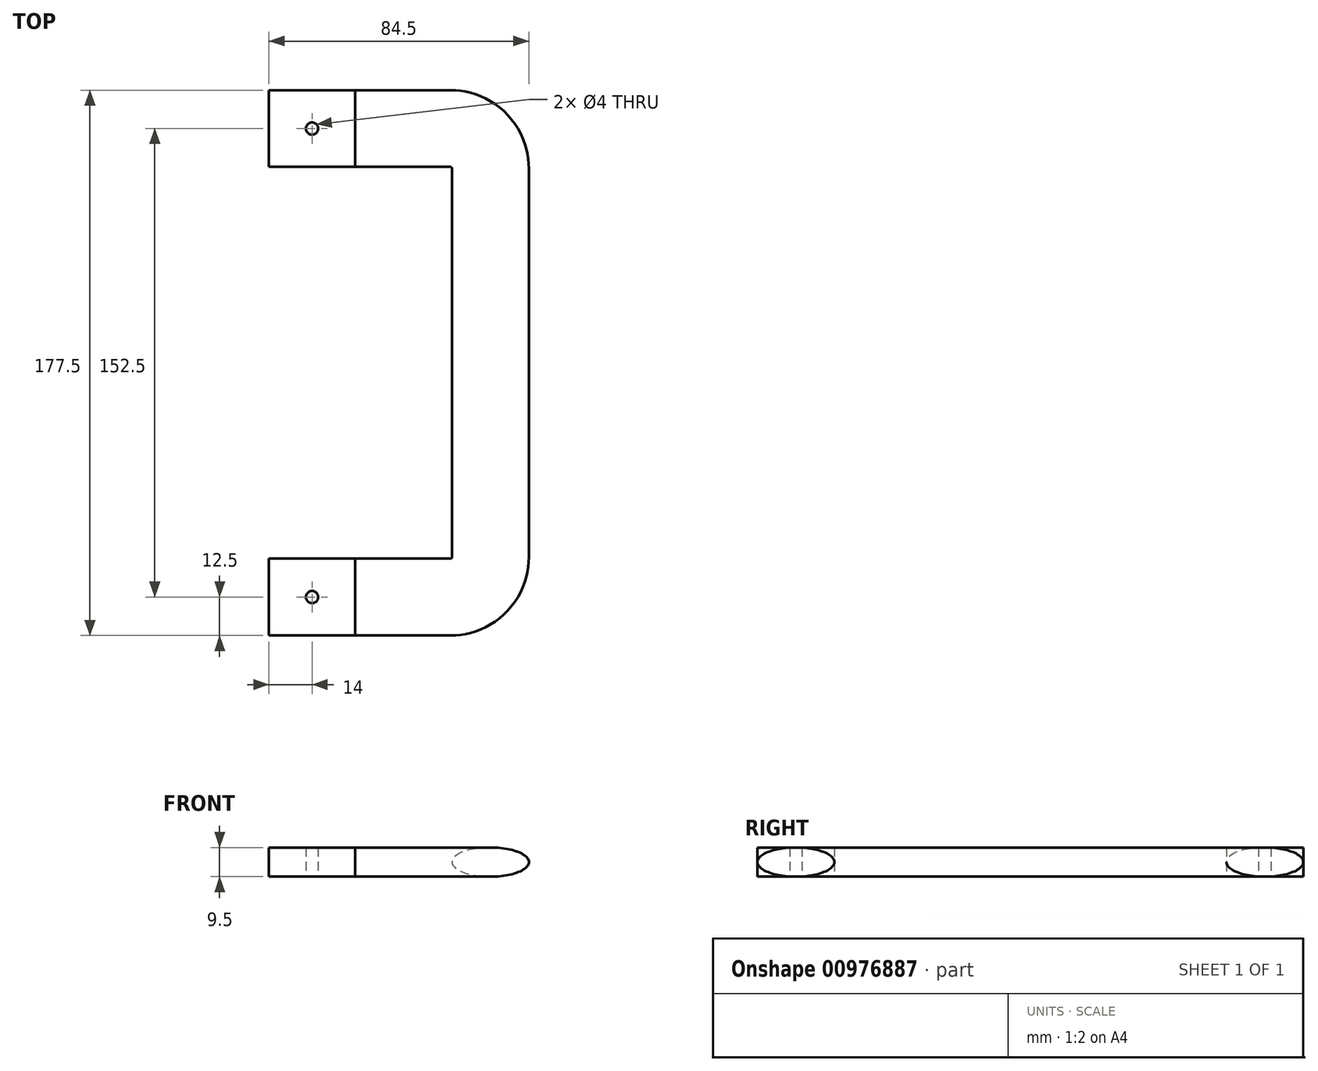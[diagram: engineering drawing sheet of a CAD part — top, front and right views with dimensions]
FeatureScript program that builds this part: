
annotation { "Feature Type Name" : "Feature", "Feature Type Description" : "" }
export const myFeature = defineFeature(function(context is Context, id is Id, definition is map)
    precondition{}
    {
        {
            var Q0;
            Q0=qCreatedBy(makeId("Top.planeOp"),FACE);
            var sketch = newSketch(context, id + "F0", { "sketchPlane" : qUnion([Q0])});
            skPoint(sketch, "E0", {"position": v(-44, 76.25) * mm});
            skPoint(sketch, "E1", {"position": v(-44, -76.25) * mm});
            skLineSegment(sketch, "E2.bottom", {"start": v(-30, 88.75) * mm, "end": v(-58, 88.75) * mm});
            skLineSegment(sketch, "E2.top", {"start": v(-30, 63.75) * mm, "end": v(-58, 63.75) * mm});
            skLineSegment(sketch, "E2.left", {"start": v(-30, 88.75) * mm, "end": v(-30, 63.75) * mm});
            skLineSegment(sketch, "E2.right", {"start": v(-58, 88.75) * mm, "end": v(-58, 63.75) * mm});
            skLineSegment(sketch, "E3.bottom", {"start": v(-30, -63.75) * mm, "end": v(-58, -63.75) * mm});
            skLineSegment(sketch, "E3.top", {"start": v(-30, -88.75) * mm, "end": v(-58, -88.75) * mm});
            skLineSegment(sketch, "E3.left", {"start": v(-30, -63.75) * mm, "end": v(-30, -88.75) * mm});
            skLineSegment(sketch, "E3.right", {"start": v(-58, -63.75) * mm, "end": v(-58, -88.75) * mm});
            skCircle(sketch, "E4", {"center": v(-44, 76.25) * mm, "radius": 2 * mm});
            skCircle(sketch, "E5", {"center": v(-44, -76.25) * mm, "radius": 2 * mm});
            skSolve(sketch);
        }
        {
            var Q0;
            Q0 = qSketchRegion(id + "F0", true);
            extrude(context, id + "F1", {"entities" : qUnion([Q0]), "endBound" : BoundingType.SYMMETRIC, "depth" : 9.5 * mm, "offsetDistance" : 25 * mm});
        }
        {
            var Q0;
            Q0=qCreatedBy(makeId("Top.planeOp"),FACE);
            var sketch = newSketch(context, id + "F2", { "sketchPlane" : qUnion([Q0])});
            skLineSegment(sketch, "E6", {"start": v(-30, 76.25) * mm, "end": v(1, 76.25) * mm});
            skLineSegment(sketch, "E7", {"start": v(14, 63.25) * mm, "end": v(14, -63.25) * mm});
            skLineSegment(sketch, "E8", {"start": v(1, -76.25) * mm, "end": v(-30, -76.25) * mm});
            skPoint(sketch, "E9.visualSharp", {"position": v(14, 76.25) * mm});
            skArc(sketch, "E9.filletArc", {"start": v(14, 63.25) * mm, "mid": v(10.2, 72.44) * mm, "end": v(1, 76.25) * mm});
            skPoint(sketch, "E10.visualSharp", {"position": v(14, -76.25) * mm});
            skArc(sketch, "E10.filletArc", {"start": v(1, -76.25) * mm, "mid": v(10.2, -72.44) * mm, "end": v(14, -63.25) * mm});
            skSolve(sketch);
        }
        {
            var Q0;
            Q0=makeQuery(id+"F1.opExtrude","SWEPT_FACE",FACE,{"disambiguationData":[OSD([sQuery(id+"F0.wireOp",EDGE,"E2.left")])]});
            var sketch = newSketch(context, id + "F3", { "sketchPlane" : qUnion([Q0])});
            skEllipse(sketch, "E11", {"center": v(76.25, 0) * mm, "majorRadius": 12.5 * mm, "minorRadius": 4.75 * mm, "majorAxis": v(1, 0)});
            skSolve(sketch);
        }
        {
            var Q0;
            Q0 = qSketchRegion(id + "F3", true);
            var Q1;
            Q1 = qConstructionFilter(qBodyType(qCreatedBy(id + "F2" ,EDGE), BodyType.WIRE), ConstructionObject.NO);
            sweep(context, id + "F4", {"operationType" : NewBodyOperationType.ADD, "profiles" : qUnion([Q0]), "path" : qUnion([Q1])});
        }
    });
